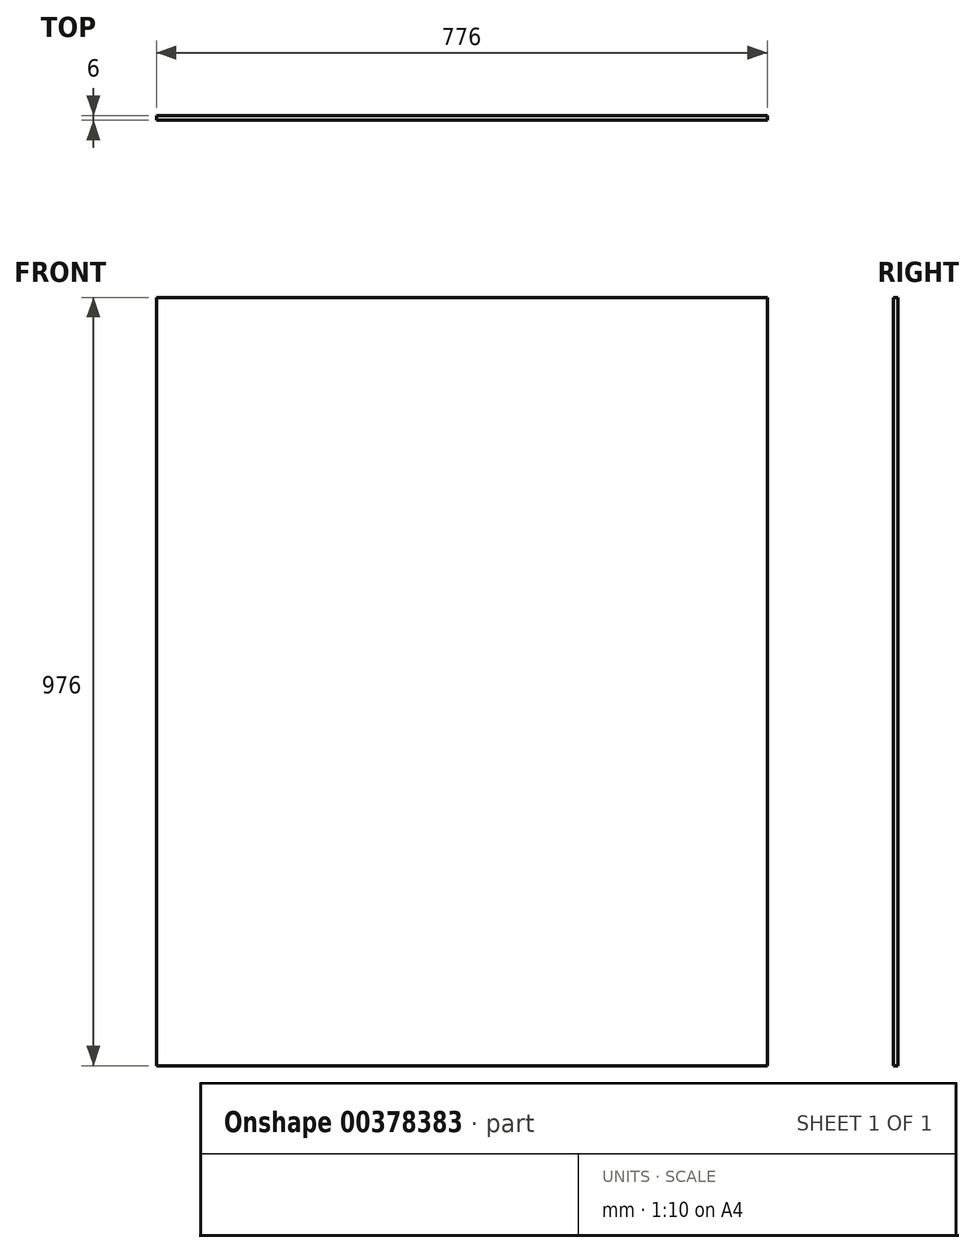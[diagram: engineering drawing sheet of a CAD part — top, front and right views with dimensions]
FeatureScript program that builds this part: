
annotation { "Feature Type Name" : "Feature", "Feature Type Description" : "" }
export const myFeature = defineFeature(function(context is Context, id is Id, definition is map)
    precondition{}
    {
        {
            var Q0;
            Q0=qCreatedBy(makeId("Front.planeOp"),FACE);
            var sketch = newSketch(context, id + "F0", { "sketchPlane" : qUnion([Q0])});
            skLineSegment(sketch, "E0.bottom", {"start": v(388, 488) * mm, "end": v(-388, 488) * mm});
            skLineSegment(sketch, "E0.top", {"start": v(388, -488) * mm, "end": v(-388, -488) * mm});
            skLineSegment(sketch, "E0.left", {"start": v(388, 488) * mm, "end": v(388, -488) * mm});
            skLineSegment(sketch, "E0.right", {"start": v(-388, 488) * mm, "end": v(-388, -488) * mm});
            skPoint(sketch, "E0.middle", {"position": v(0, 0) * mm});
            skSolve(sketch);
        }
        {
            var Q0;
            Q0=qSketchRegion(id+"F0",true);
            extrude(context, id + "F1", {"entities" : qUnion([Q0]), "depth" : 6 * mm});
        }
    });
